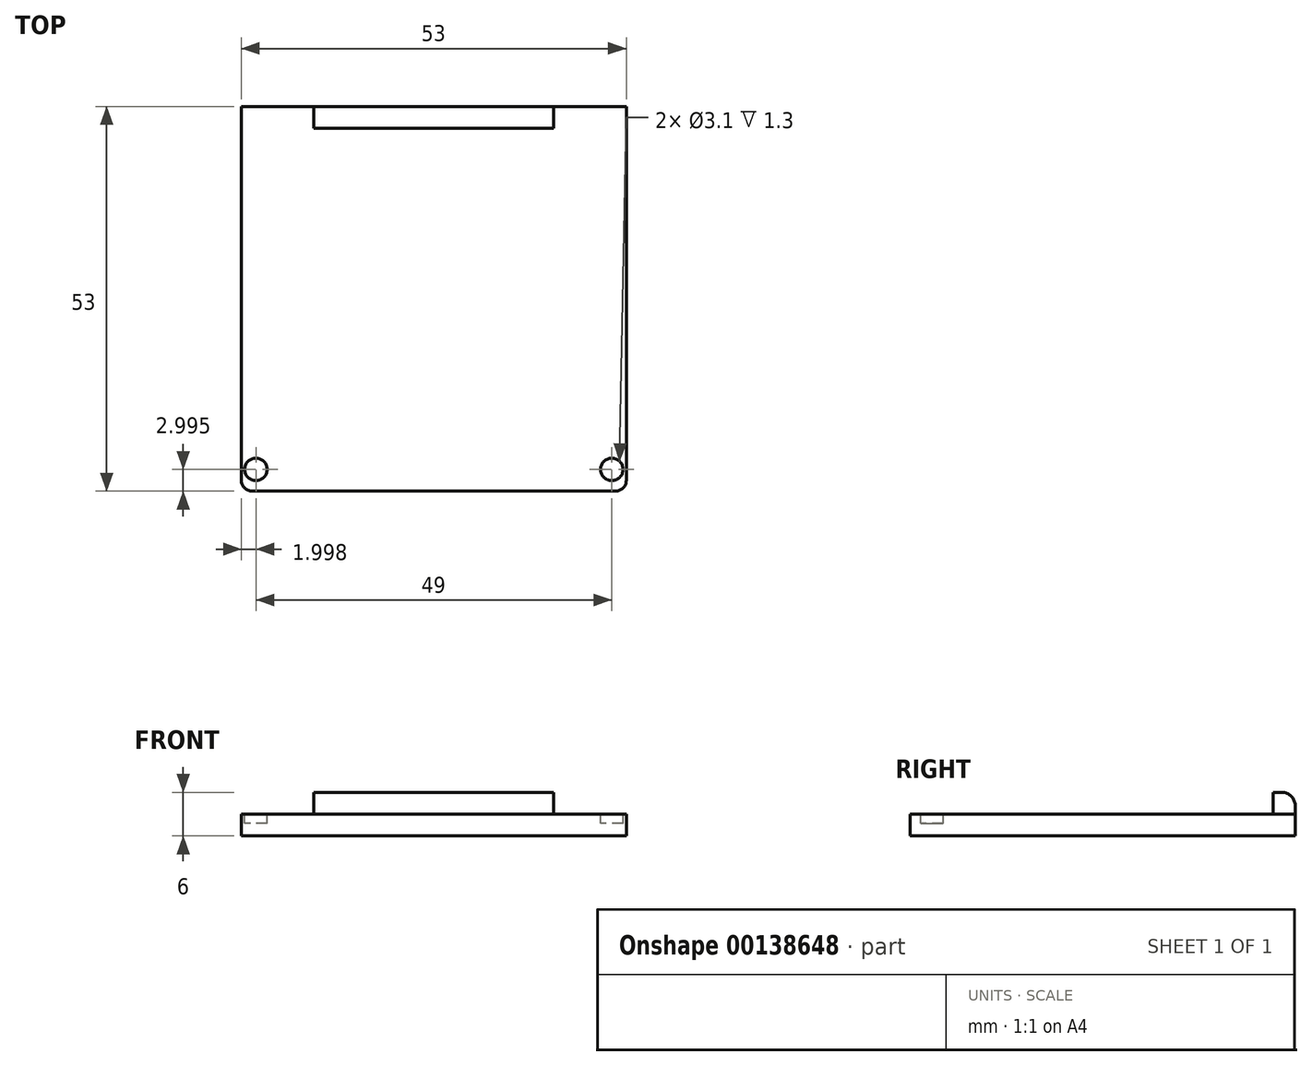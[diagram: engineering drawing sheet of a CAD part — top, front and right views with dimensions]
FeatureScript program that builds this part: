
annotation { "Feature Type Name" : "Feature", "Feature Type Description" : "" }
export const myFeature = defineFeature(function(context is Context, id is Id, definition is map)
    precondition{}
    {
        {
            var Q0;
            Q0=qCreatedBy(makeId("Top.planeOp"),FACE);
            var sketch = newSketch(context, id + "F0", { "sketchPlane" : qUnion([Q0])});
            skLineSegment(sketch, "E0.bottom", {"start": v(-26.4, 27) * mm, "end": v(26.6, 27) * mm});
            skLineSegment(sketch, "E0.top", {"start": v(-26.4, -26) * mm, "end": v(26.6, -26) * mm});
            skLineSegment(sketch, "E0.left", {"start": v(-26.4, 27) * mm, "end": v(-26.4, -26) * mm});
            skLineSegment(sketch, "E0.right", {"start": v(26.6, 27) * mm, "end": v(26.6, -26) * mm});
            skSolve(sketch);
        }
        {
            var Q0;
            Q0 = qSketchRegion(id + "F0", true);
            extrude(context, id + "F1", {"entities" : qUnion([Q0]), "depth" : 3 * mm});
        }
        {
            var Q0;
            Q0=makeQuery(id+"F1.opExtrude","CAP_FACE",FACE,{"disambiguationData":[OSD([sQuery(id+"F0.wireOp",EDGE,"E0.bottom"),sQuery(id+"F0.wireOp",EDGE,"E0.top"),sQuery(id+"F0.wireOp",EDGE,"E0.left"),sQuery(id+"F0.wireOp",EDGE,"E0.right")])],"isStart":false});
            var sketch = newSketch(context, id + "F2", { "sketchPlane" : qUnion([Q0])});
            skLineSegment(sketch, "E1.bottom", {"start": v(-24.4, 24) * mm, "end": v(24.6, 24) * mm});
            skLineSegment(sketch, "E1.top", {"start": v(-24.4, -23) * mm, "end": v(24.6, -23) * mm});
            skLineSegment(sketch, "E1.left", {"start": v(-24.4, 24) * mm, "end": v(-24.4, -23) * mm});
            skLineSegment(sketch, "E1.right", {"start": v(24.6, 24) * mm, "end": v(24.6, -23) * mm});
            skCircle(sketch, "E2", {"center": v(24.6, -23) * mm, "radius": 1.55 * mm});
            skCircle(sketch, "E3", {"center": v(-24.4, -23) * mm, "radius": 1.55 * mm});
            skSolve(sketch);
        }
        {
            var Q0;
            {var subQ0=sQuery(id+"F2.wireOp",EDGE,"E1.left");var subQ1=sQuery(id+"F2.wireOp",EDGE,"E1.top");var subQ2=makeQuery(id+"F2.imprint","INTERSECT",VERTEX,{"derivedFrom":[subQ1,subQ0]});Q0=makeQuery(id+"F2.imprint","IMPRINT",FACE,{"disambiguationData":[TD([[makeQuery(id+"F2.imprint","IMPRINT",EDGE,{"disambiguationData":[TD([[subQ2,-1.0]])],"derivedFrom":subQ1}),-1.0]])]});}
            var Q1;
            {var subQ0=sQuery(id+"F2.wireOp",EDGE,"E1.right");var subQ1=sQuery(id+"F2.wireOp",EDGE,"E1.top");var subQ2=makeQuery(id+"F2.imprint","INTERSECT",VERTEX,{"derivedFrom":[subQ1,subQ0]});Q1=makeQuery(id+"F2.imprint","IMPRINT",FACE,{"disambiguationData":[TD([[makeQuery(id+"F2.imprint","IMPRINT",EDGE,{"disambiguationData":[TD([[subQ2,1.0]])],"derivedFrom":subQ1}),-1.0]])]});}
            var Q2;
            {var subQ0=sQuery(id+"F2.wireOp",EDGE,"E1.right");var subQ1=sQuery(id+"F2.wireOp",EDGE,"E1.top");var subQ2=makeQuery(id+"F2.imprint","INTERSECT",VERTEX,{"derivedFrom":[subQ1,subQ0]});Q2=makeQuery(id+"F2.imprint","IMPRINT",FACE,{"disambiguationData":[TD([[makeQuery(id+"F2.imprint","IMPRINT",EDGE,{"disambiguationData":[TD([[subQ2,1.0]])],"derivedFrom":subQ1}),1.0]])]});}
            var Q3;
            {var subQ0=sQuery(id+"F2.wireOp",EDGE,"E1.left");var subQ1=sQuery(id+"F2.wireOp",EDGE,"E1.top");var subQ2=makeQuery(id+"F2.imprint","INTERSECT",VERTEX,{"derivedFrom":[subQ1,subQ0]});Q3=makeQuery(id+"F2.imprint","IMPRINT",FACE,{"disambiguationData":[TD([[makeQuery(id+"F2.imprint","IMPRINT",EDGE,{"disambiguationData":[TD([[subQ2,-1.0]])],"derivedFrom":subQ1}),1.0]])]});}
            extrude(context, id + "F3", {"entities" : qUnion([Q0, Q1, Q2, Q3]), "operationType" : NewBodyOperationType.REMOVE, "oppositeDirection" : true, "depth" : 1.3 * mm});
        }
        {
            var Q0;
            Q0=makeQuery(id+"F1.opExtrude","CAP_FACE",FACE,{"disambiguationData":[OSD([sQuery(id+"F0.wireOp",EDGE,"E0.bottom"),sQuery(id+"F0.wireOp",EDGE,"E0.top"),sQuery(id+"F0.wireOp",EDGE,"E0.left"),sQuery(id+"F0.wireOp",EDGE,"E0.right")])],"isStart":false});
            var sketch = newSketch(context, id + "F4", { "sketchPlane" : qUnion([Q0])});
            skLineSegment(sketch, "E4.bottom", {"start": v(-16.4, 27) * mm, "end": v(16.6, 27) * mm});
            skLineSegment(sketch, "E4.top", {"start": v(-16.4, 24) * mm, "end": v(16.6, 24) * mm});
            skLineSegment(sketch, "E4.left", {"start": v(-16.4, 27) * mm, "end": v(-16.4, 24) * mm});
            skLineSegment(sketch, "E4.right", {"start": v(16.6, 27) * mm, "end": v(16.6, 24) * mm});
            skSolve(sketch);
        }
        {
            var Q0;
            Q0 = qSketchRegion(id + "F4", true);
            extrude(context, id + "F5", {"entities" : qUnion([Q0]), "operationType" : NewBodyOperationType.ADD, "depth" : 3 * mm});
        }
        {
            var Q0;
            Q0=makeQuery(id+"F5.opExtrude","CAP_EDGE",EDGE,{"disambiguationData":[OSD([sQuery(id+"F4.wireOp",EDGE,"E4.bottom")])],"isStart":false});
            fillet(context, id + "F6", {"entities" : qUnion([Q0]), "radius" : 1.8 * mm, "tangentPropagation" : true, "allowEdgeOverflow" : false});
        }
        {
            var Q0;
            Q0=makeQuery(id+"F1.opExtrude","SWEPT_EDGE",EDGE,{"disambiguationData":[OSD([sQuery(id+"F0.wireOp",EDGE,"E0.top"),sQuery(id+"F0.wireOp",EDGE,"E0.right")])]});
            var Q1;
            Q1=makeQuery(id+"F1.opExtrude","SWEPT_EDGE",EDGE,{"disambiguationData":[OSD([sQuery(id+"F0.wireOp",EDGE,"E0.top"),sQuery(id+"F0.wireOp",EDGE,"E0.left")])]});
            fillet(context, id + "F7", {"entities" : qUnion([Q0, Q1]), "radius" : 1.5 * mm, "tangentPropagation" : true, "allowEdgeOverflow" : false});
        }
    });
